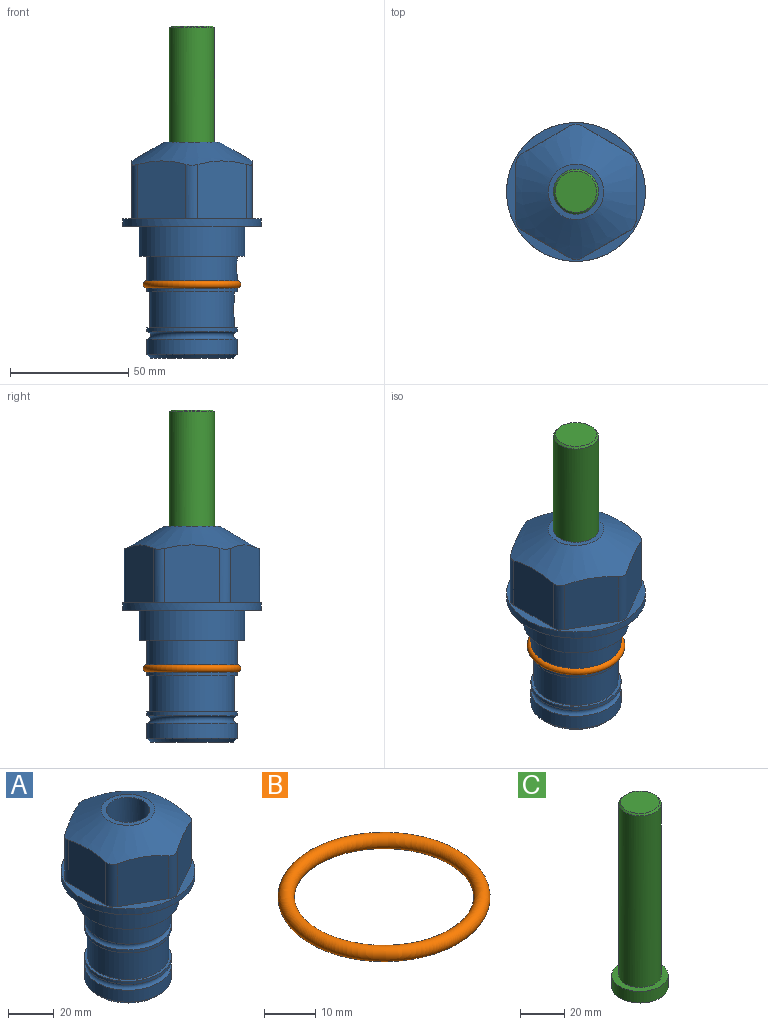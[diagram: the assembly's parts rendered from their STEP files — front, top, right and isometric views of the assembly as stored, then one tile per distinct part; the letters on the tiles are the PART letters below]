
ASSEMBLY  parts=3 mates=1
PART A: 36 faces, bbox 58.7x58.7x91.2 mm
  f0: cylinder r=17.78mm len=35.56mm, axis (0,0,1), area 1670.8mm2, adj f23,f24,f31
  f1: cylinder r=19.05mm len=38.1mm, axis (0,0,1), area 1191.9mm2, adj f26,f27,f30
  f2: plane 58.66x58.66mm, normal (0,0,-1), area 1150.6mm2, adj f3,f28
  f3: cylinder r=29.33mm len=58.66mm, axis (0,0,-1), area 585.1mm2, adj f2,f4
  f4: plane 58.66x58.66mm, normal (0,0,1), area 475.9mm2, adj f3,f5,f6,f7,f8,f9,f10,f11
  f5: plane 24.5x20.32mm, normal (-0.5,0.87,0), area 562.8mm2, adj f4,f15,f16,f17
  f6: plane 24.5x20.32mm, normal (0.5,0.87,0), area 562.8mm2, adj f4,f14,f15,f17
  f7: plane 24.5x23.48mm, normal (1,0,0), area 562.8mm2, adj f4,f13,f14,f17
  f8: plane 24.5x20.32mm, normal (0.5,-0.87,0), area 562.8mm2, adj f4,f12,f13,f17
  f9: plane 24.5x20.32mm, normal (-0.5,-0.87,0), area 562.8mm2, adj f4,f11,f12,f17
  f10: plane 24.5x23.48mm, normal (-1,0,0), area 562.8mm2, adj f4,f11,f16,f17
  f11: cylinder r=5.08mm len=23.01mm, axis (0,0,-1), area 121.2mm2, adj f4,f9,f10,f17
  f12: cylinder r=5.08mm len=23.01mm, axis (0,0,-1), area 121.2mm2, adj f4,f8,f9,f17
  f13: cylinder r=5.08mm len=23.01mm, axis (0,0,-1), area 121.2mm2, adj f4,f7,f8,f17
  f14: cylinder r=5.08mm len=23.01mm, axis (0,0,-1), area 121.2mm2, adj f4,f6,f7,f17
  f15: cylinder r=5.08mm len=23.01mm, axis (0,0,-1), area 121.2mm2, adj f4,f5,f6,f17
  f16: cylinder r=5.08mm len=23.01mm, axis (0,0,-1), area 121.2mm2, adj f4,f5,f10,f17
  f17: cone r=11.73mm half-angle=60deg, axis (0,0,-1), area 2071.8mm2, adj f5,f6,f7,f8,f9,f10,f11,f12
  f18: plane 23.46x23.46mm, normal (0,0,1), area 147.4mm2, adj f17,f35
  f19: plane 34.93x34.93mm, normal (0,0,-1), area 958mm2, adj f29
  f20: cylinder r=19.05mm len=38.1mm, axis (0,0,1), area 760.1mm2, adj f21,f29
  f21: torus R=19.05mm, axis (0,0,1), area 565.3mm2, adj f20,f22
  f22: cylinder r=19.05mm len=38.1mm, axis (0,0,1), area 190mm2, adj f21,f23
  f23: plane 38.1x38.1mm, normal (0,0,1), area 146.9mm2, adj f0,f22
  f24: plane 38.1x38.1mm, normal (0,0,-1), area 146.9mm2, adj f0,f25
  f25: cylinder r=19.05mm len=38.1mm, axis (0,0,1), area 190mm2, adj f24,f26
  f26: torus R=19.05mm, axis (0,0,1), area 565.3mm2, adj f1,f25
  f27: plane 44.45x44.45mm, normal (0,0,-1), area 411.7mm2, adj f1,f28
  f28: cylinder r=22.23mm len=44.45mm, axis (0,0,1), area 1773.5mm2, adj f2,f27
  f29: cone r=19.05mm half-angle=45deg, axis (0,0,1), area 257.5mm2, adj f19,f20
  f30: cylinder r=3.17mm len=6.75mm, axis (-1,0,0), area 128mm2, adj f1,f33
  f31: cylinder r=3.17mm len=6.35mm, axis (-1,0,0), area 102.5mm2, adj f0,f33
  f32: plane 25.4x25.4mm, normal (0,0,1), area 506.7mm2, adj f33
  f33: cylinder r=12.7mm len=66.42mm, axis (0,0,-1), area 5236.2mm2, adj f30,f31,f32,f34
  f34: cone r=9.53mm half-angle=30deg, axis (0,0,-1), area 443.4mm2, adj f33,f35
  f35: cylinder r=9.53mm len=19.05mm, axis (0,0,-1), area 849mm2, adj f18,f34
PART B: 1 faces, bbox 44.7x44.7x3.2 mm
  f0: torus R=19.05mm, axis (0,0,1), area 1193.9mm2
PART C: 6 faces, bbox 25.4x25.4x101.6 mm
  f0: plane 17.46x17.46mm, normal (0,0,1), area 239.5mm2, adj f5
  f1: plane 25.4x25.4mm, normal (0,0,-1), area 506.7mm2, adj f2
  f2: cylinder r=12.7mm len=25.4mm, axis (0,0,1), area 506.7mm2, adj f1,f3
  f3: plane 25.4x25.4mm, normal (0,0,1), area 221.7mm2, adj f2,f4
  f4: cylinder r=9.53mm len=94.46mm, axis (0,0,1), area 5653mm2, adj f3,f5
  f5: cone r=8.73mm half-angle=45deg, axis (0,0,-1), area 64.4mm2, adj f0,f4
PLACE A at identity fixed
PLACE B at identity
PLACE C rot(axis=(0,0,1),0deg) t=(0,0,11.01)mm
MATE cylindrical C.f2 <-> A.f0  axis (0,0,1) through (0,0,36.65)mm
